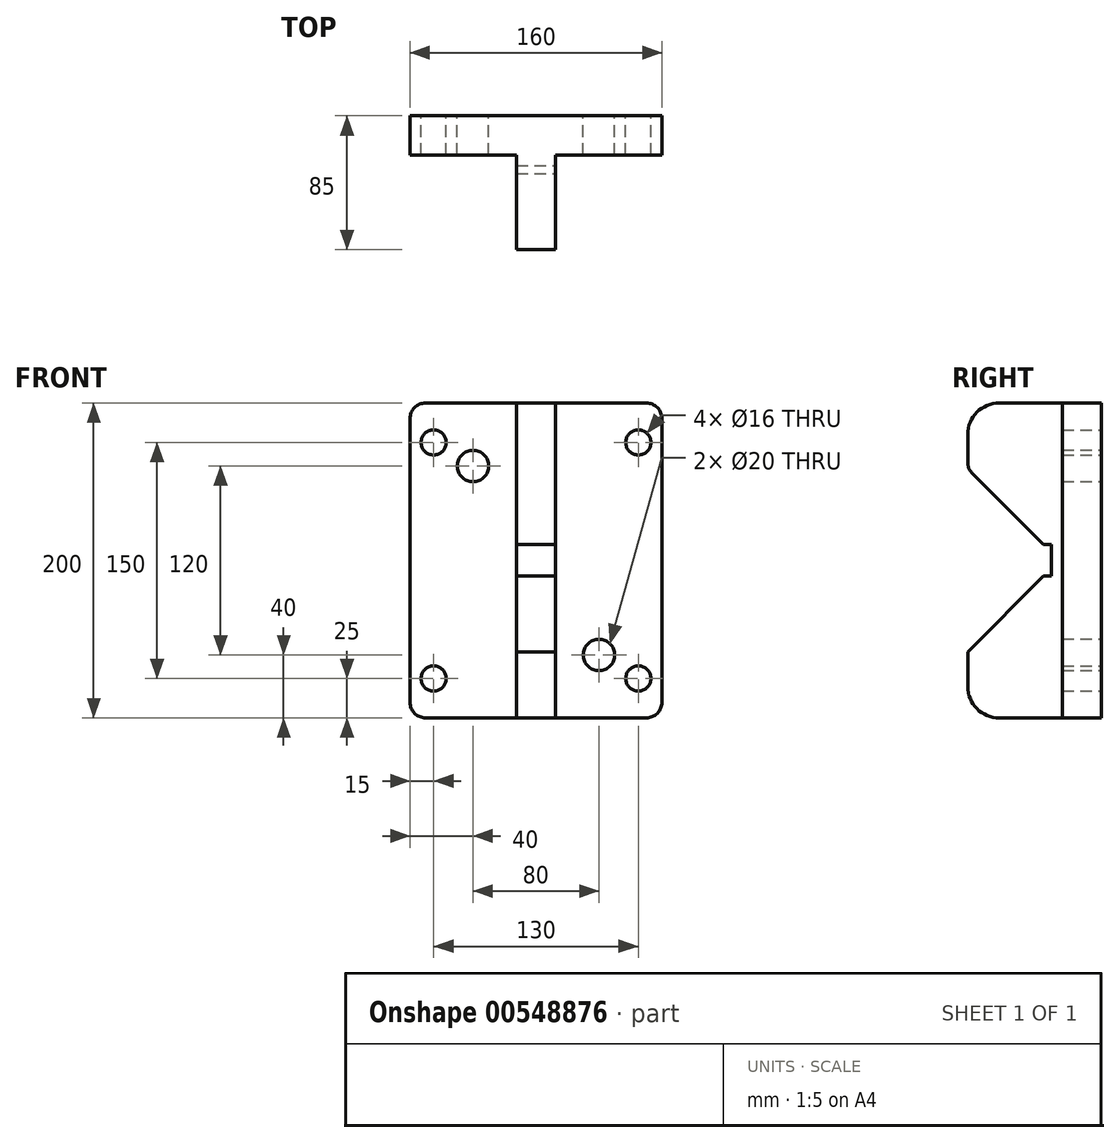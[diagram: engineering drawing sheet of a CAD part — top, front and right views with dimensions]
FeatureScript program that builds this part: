
annotation { "Feature Type Name" : "Feature", "Feature Type Description" : "" }
export const myFeature = defineFeature(function(context is Context, id is Id, definition is map)
    precondition{}
    {
        {
            var Q0;
            Q0=qCreatedBy(makeId("Front.planeOp"),FACE);
            var sketch = newSketch(context, id + "F0", { "sketchPlane" : qUnion([Q0])});
            skLineSegment(sketch, "E0.bottom", {"start": v(-80, 100) * mm, "end": v(80, 100) * mm});
            skLineSegment(sketch, "E0.top", {"start": v(-80, -100) * mm, "end": v(80, -100) * mm});
            skLineSegment(sketch, "E0.left", {"start": v(-80, 100) * mm, "end": v(-80, -100) * mm});
            skLineSegment(sketch, "E0.right", {"start": v(80, 100) * mm, "end": v(80, -100) * mm});
            skPoint(sketch, "E0.middle", {"position": v(0, 0) * mm});
            skLineSegment(sketch, "E1.bottom", {"start": v(-12.5, 100) * mm, "end": v(12.5, 100) * mm});
            skLineSegment(sketch, "E1.top", {"start": v(-12.5, -100) * mm, "end": v(12.5, -100) * mm});
            skLineSegment(sketch, "E1.left", {"start": v(-12.5, 100) * mm, "end": v(-12.5, -100) * mm, "construction": true});
            skLineSegment(sketch, "E1.right", {"start": v(12.5, 100) * mm, "end": v(12.5, -100) * mm, "construction": true});
            skLineSegment(sketch, "E2", {"start": v(0, 0) * mm, "end": v(0, 100) * mm, "construction": true});
            skLineSegment(sketch, "E3", {"start": v(0, 100) * mm, "end": v(0, 0) * mm, "construction": true});
            skLineSegment(sketch, "E4", {"start": v(0, -100) * mm, "end": v(0, 0) * mm, "construction": true});
            skLineSegment(sketch, "E5", {"start": v(0, 0) * mm, "end": v(-80, 0) * mm, "construction": true});
            skLineSegment(sketch, "E6", {"start": v(-80, 0) * mm, "end": v(0, 0) * mm, "construction": true});
            skLineSegment(sketch, "E7", {"start": v(80, 0) * mm, "end": v(0, 0) * mm, "construction": true});
            skCircle(sketch, "E8", {"center": v(-65, 75) * mm, "radius": 8 * mm});
            skCircle(sketch, "E9", {"center": v(-40, 60) * mm, "radius": 10 * mm});
            skCircle(sketch, "E10.MirrorC", {"center": v(-65, -75) * mm, "radius": 8 * mm});
            skCircle(sketch, "E11.MirrorC", {"center": v(65, -75) * mm, "radius": 8 * mm});
            skCircle(sketch, "E12.MirrorC", {"center": v(65, 75) * mm, "radius": 8 * mm});
            skCircle(sketch, "E13", {"center": v(40, -60) * mm, "radius": 10 * mm});
            skSolve(sketch);
        }
        {
            var Q0;
            Q0 = qSketchRegion(id + "F0", true);
            extrude(context, id + "F1", {"entities" : qUnion([Q0]), "depth" : 25 * mm, "offsetDistance" : 25 * mm});
        }
        {
            var Q0;
            Q0=makeQuery(id+"F1.opExtrude","CAP_FACE",FACE,{"disambiguationData":[OSD([sQuery(id+"F0.wireOp",EDGE,"E0.bottom"),sQuery(id+"F0.wireOp",EDGE,"E0.top"),sQuery(id+"F0.wireOp",EDGE,"E0.left"),sQuery(id+"F0.wireOp",EDGE,"E0.right"),sQuery(id+"F0.wireOp",EDGE,"E1.bottom"),sQuery(id+"F0.wireOp",EDGE,"E1.top"),sQuery(id+"F0.wireOp",EDGE,"E8"),sQuery(id+"F0.wireOp",EDGE,"E9"),sQuery(id+"F0.wireOp",EDGE,"E10.MirrorC"),sQuery(id+"F0.wireOp",EDGE,"E11.MirrorC"),sQuery(id+"F0.wireOp",EDGE,"E12.MirrorC"),sQuery(id+"F0.wireOp",EDGE,"E13")])],"isStart":false});
            var sketch = newSketch(context, id + "F2", { "sketchPlane" : qUnion([Q0])});
            skLineSegment(sketch, "E14.bottom", {"start": v(-12.5, 100) * mm, "end": v(12.5, 100) * mm});
            skLineSegment(sketch, "E14.top", {"start": v(-12.5, -100) * mm, "end": v(12.5, -100) * mm});
            skLineSegment(sketch, "E14.left", {"start": v(-12.5, 100) * mm, "end": v(-12.5, -100) * mm});
            skLineSegment(sketch, "E14.right", {"start": v(12.5, 100) * mm, "end": v(12.5, -100) * mm});
            skPoint(sketch, "E14.middle", {"position": v(0, 0) * mm});
            skSolve(sketch);
        }
        {
            var Q0;
            Q0=makeQuery(id+"F2.imprint","IMPRINT",FACE,{"disambiguationData":[TD([[makeQuery(id+"F2.imprint","IMPRINT",EDGE,{"derivedFrom":sQuery(id+"F2.wireOp",EDGE,"E14.bottom")}),-1.0]])]});
            extrude(context, id + "F3", {"entities" : qUnion([Q0]), "operationType" : NewBodyOperationType.ADD, "depth" : 60 * mm, "offsetDistance" : 25 * mm});
        }
        {
            var Q0;
            Q0=makeQuery(id+"F3.opExtrude","SWEPT_FACE",FACE,{"disambiguationData":[OSD([sQuery(id+"F2.wireOp",EDGE,"E14.right")])]});
            var sketch = newSketch(context, id + "F4", { "sketchPlane" : qUnion([Q0])});
            skLineSegment(sketch, "E15", {"start": v(-55, 100) * mm, "end": v(-55, -100) * mm, "construction": true});
            skLineSegment(sketch, "E16", {"start": v(-85, 0) * mm, "end": v(-25, 0) * mm, "construction": true});
            skLineSegment(sketch, "E17", {"start": v(-85, 58.24) * mm, "end": v(-36.76, 10) * mm});
            skLineSegment(sketch, "E18", {"start": v(-36.76, 10) * mm, "end": v(-31.76, 10) * mm});
            skLineSegment(sketch, "E19", {"start": v(-31.76, 10) * mm, "end": v(-31.76, 0) * mm});
            skLineSegment(sketch, "E20", {"start": v(-31.76, 0) * mm, "end": v(-85, 0) * mm, "construction": true});
            skLineSegment(sketch, "E21.MirrorCS", {"start": v(-85, -58.24) * mm, "end": v(-36.76, -10) * mm});
            skLineSegment(sketch, "E22.MirrorCS", {"start": v(-31.76, -10) * mm, "end": v(-31.76, 0) * mm});
            skLineSegment(sketch, "E23.MirrorCS", {"start": v(-36.76, -10) * mm, "end": v(-31.76, -10) * mm});
            skSolve(sketch);
        }
        {
            var Q0;
            {var subQ1=sQuery(id+"F4.wireOp",EDGE,"E17");Q0=makeQuery(id+"F4.imprint","IMPRINT",FACE,{"disambiguationData":[TD([[makeQuery(id+"F4.imprint","IMPRINT",EDGE,{"derivedFrom":subQ1}),-1.0]])]});}
            extrude(context, id + "F5", {"entities" : qUnion([Q0]), "operationType" : NewBodyOperationType.REMOVE, "oppositeDirection" : true, "depth" : 25 * mm, "offsetDistance" : 25 * mm});
        }
        {
            var Q0;
            Q0=makeQuery(id+"F1.opExtrude","SWEPT_EDGE",EDGE,{"disambiguationData":[OSD([sQuery(id+"F0.wireOp",EDGE,"E0.bottom"),sQuery(id+"F0.wireOp",EDGE,"E0.right")])]});
            var Q1;
            Q1=makeQuery(id+"F1.opExtrude","SWEPT_EDGE",EDGE,{"disambiguationData":[OSD([sQuery(id+"F0.wireOp",EDGE,"E0.bottom"),sQuery(id+"F0.wireOp",EDGE,"E0.left")])]});
            var Q2;
            Q2=makeQuery(id+"F1.opExtrude","SWEPT_EDGE",EDGE,{"disambiguationData":[OSD([sQuery(id+"F0.wireOp",EDGE,"E0.top"),sQuery(id+"F0.wireOp",EDGE,"E0.left")])]});
            var Q3;
            Q3=makeQuery(id+"F1.opExtrude","SWEPT_EDGE",EDGE,{"disambiguationData":[OSD([sQuery(id+"F0.wireOp",EDGE,"E0.top"),sQuery(id+"F0.wireOp",EDGE,"E0.right")])]});
            fillet(context, id + "F6", {"entities" : qUnion([Q0, Q1, Q2, Q3]), "radius" : 10 * mm, "tangentPropagation" : true, "allowEdgeOverflow" : false});
        }
        {
            var Q0;
            Q0=makeQuery(id+"F3.opExtrude","CAP_EDGE",EDGE,{"disambiguationData":[OSD([sQuery(id+"F2.wireOp",EDGE,"E14.top")])],"isStart":false});
            var Q1;
            Q1=makeQuery(id+"F3.opExtrude","CAP_EDGE",EDGE,{"disambiguationData":[OSD([sQuery(id+"F2.wireOp",EDGE,"E14.bottom")])],"isStart":false});
            fillet(context, id + "F7", {"entities" : qUnion([Q0, Q1]), "radius" : 20 * mm, "tangentPropagation" : true, "allowEdgeOverflow" : false});
        }
        {
            var Q0;
            Q0=makeQuery(id+"F5.boolean.opBoolean","COPY",EDGE,{"derivedFrom":makeQuery(id+"F5.opExtrude","SWEPT_EDGE",EDGE,{"disambiguationData":[OSD([sQuery(id+"F2.wireOp",EDGE,"E14.right"),sQuery(id+"F4.wireOp",EDGE,"E21.MirrorCS")])]})});
            var Q1;
            Q1=makeQuery(id+"F5.boolean.opBoolean","COPY",EDGE,{"derivedFrom":makeQuery(id+"F5.opExtrude","SWEPT_EDGE",EDGE,{"disambiguationData":[OSD([sQuery(id+"F2.wireOp",EDGE,"E14.right"),sQuery(id+"F4.wireOp",EDGE,"E17")])]})});
            fillet(context, id + "F8", {"entities" : qUnion([Q0, Q1]), "radius" : 10 * mm, "tangentPropagation" : true, "allowEdgeOverflow" : false});
        }
    });
